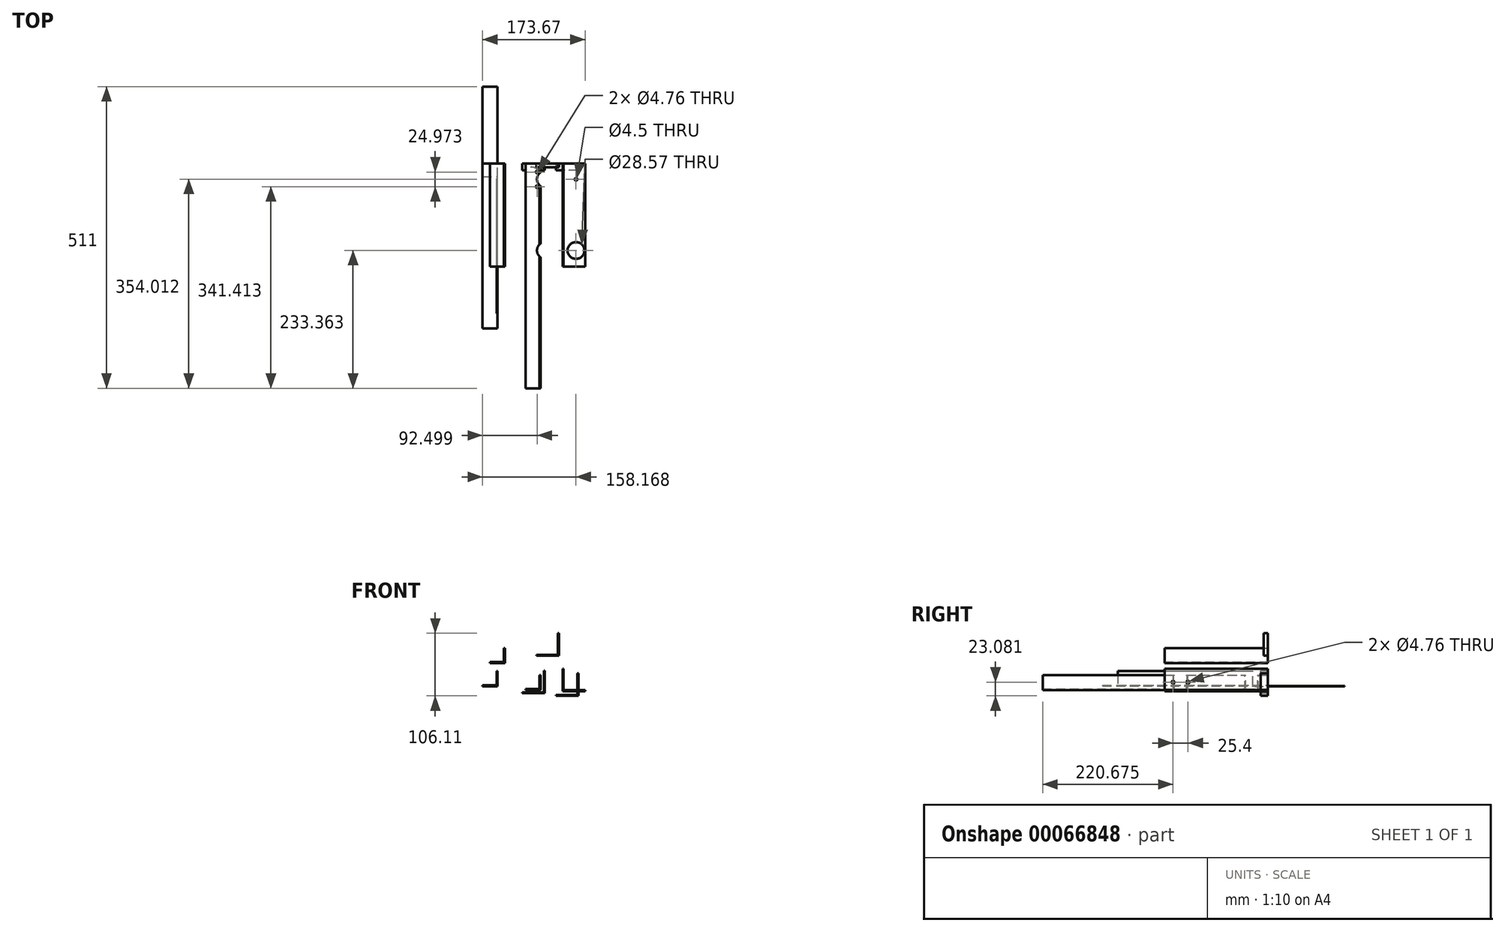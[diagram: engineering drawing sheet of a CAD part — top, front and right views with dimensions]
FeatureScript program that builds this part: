
annotation { "Feature Type Name" : "Feature", "Feature Type Description" : "" }
export const myFeature = defineFeature(function(context is Context, id is Id, definition is map)
    precondition{}
    {
        {
            assignVariable(context, id + "F0", {"name" : "angshooterl", "anyValue" : 12});
        }
        {
            var Q0;
            Q0=qCreatedBy(makeId("Front.planeOp"),FACE);
            var sketch = newSketch(context, id + "F1", { "sketchPlane" : qUnion([Q0])});
            skLineSegment(sketch, "E0.rect.bottom", {"start": v(12.7, 0.8) * mm, "end": v(-12.7, 0.8) * mm});
            skLineSegment(sketch, "E0.rect.top", {"start": v(12.7, -0.8) * mm, "end": v(-12.7, -0.8) * mm});
            skLineSegment(sketch, "E0.rect.left", {"start": v(12.7, 0.8) * mm, "end": v(12.7, -0.8) * mm});
            skLineSegment(sketch, "E0.rect.right", {"start": v(-12.7, 0.8) * mm, "end": v(-12.7, -0.8) * mm});
            skPoint(sketch, "E0.rect.middle", {"position": v(0, 0) * mm});
            skLineSegment(sketch, "E1.bottom", {"start": v(12.7, -0.8) * mm, "end": v(11.11, -0.8) * mm});
            skLineSegment(sketch, "E1.top", {"start": v(12.7, 24.6) * mm, "end": v(11.11, 24.6) * mm});
            skLineSegment(sketch, "E1.left", {"start": v(12.7, -0.8) * mm, "end": v(12.7, 24.6) * mm});
            skLineSegment(sketch, "E1.right", {"start": v(11.11, -0.8) * mm, "end": v(11.11, 24.6) * mm});
            skSolve(sketch);
        }
        {
            var Q0;
            Q0 = qSketchRegion(id + "F1", true);
            extrude(context, id + "F2", {"entities" : qUnion([Q0]), "depth" : 381 * mm});
        }
        {
            var Q0;
            Q0=qCreatedBy(makeId("Front.planeOp"),FACE);
            var sketch = newSketch(context, id + "F3", { "sketchPlane" : qUnion([Q0])});
            skLineSegment(sketch, "E2.rect.bottom", {"start": v(20.1, -4.5) * mm, "end": v(-18, -4.5) * mm});
            skLineSegment(sketch, "E2.rect.top", {"start": v(20.1, -6.09) * mm, "end": v(-18, -6.09) * mm});
            skLineSegment(sketch, "E2.rect.left", {"start": v(20.1, -4.5) * mm, "end": v(20.1, -6.09) * mm});
            skLineSegment(sketch, "E2.rect.right", {"start": v(-18, -4.5) * mm, "end": v(-18, -6.09) * mm});
            skPoint(sketch, "E2.rect.middle", {"position": v(1.06, -5.3) * mm});
            skLineSegment(sketch, "E3.bottom", {"start": v(20.1, -6.09) * mm, "end": v(18.52, -6.09) * mm});
            skLineSegment(sketch, "E3.top", {"start": v(20.1, 32.01) * mm, "end": v(18.52, 32.01) * mm});
            skLineSegment(sketch, "E3.left", {"start": v(20.1, -6.09) * mm, "end": v(20.1, 32.01) * mm});
            skLineSegment(sketch, "E3.right", {"start": v(18.52, -6.09) * mm, "end": v(18.52, 32.01) * mm});
            skSolve(sketch);
        }
        {
            var Q0;
            Q0 = qSketchRegion(id + "F3", true);
            extrude(context, id + "F4", {"entities" : qUnion([Q0]), "depth" : (getVariable(context, 'angshooterl')) * mm});
        }
        {
            var Q0;
            Q0=makeQuery(id+"F4.opExtrude","SWEPT_FACE",FACE,{"disambiguationData":[OSD([sQuery(id+"F3.wireOp",EDGE,"E2.rect.bottom")])]});
            var sketch = newSketch(context, id + "F5", { "sketchPlane" : qUnion([Q0])});
            skCircle(sketch, "E4", {"center": v(-2.48, -20.64) * mm, "radius": 14.29 * mm});
            skCircle(sketch, "E5", {"center": v(-2.36, -128.14) * mm, "radius": 14.29 * mm});
            skCircle(sketch, "E6", {"center": v(-1.24, -248.79) * mm, "radius": 14.29 * mm});
            skSolve(sketch);
        }
        {
            var Q0;
            Q0 = qSketchRegion(id + "F5", true);
            extrude(context, id + "F6", {"entities" : qUnion([Q0]), "operationType" : NewBodyOperationType.REMOVE, "endBound" : BoundingType.THROUGH_ALL, "oppositeDirection" : true, "depth" : 25.4 * mm});
        }
        {
            var Q0;
            Q0=qCreatedBy(makeId("Front.planeOp"),FACE);
            var sketch = newSketch(context, id + "F7", { "sketchPlane" : qUnion([Q0])});
            skLineSegment(sketch, "E7.rect.bottom", {"start": v(76.98, -8.97) * mm, "end": v(38.88, -8.97) * mm});
            skLineSegment(sketch, "E7.rect.top", {"start": v(76.98, -10.56) * mm, "end": v(38.88, -10.56) * mm});
            skLineSegment(sketch, "E7.rect.left", {"start": v(76.98, -8.97) * mm, "end": v(76.98, -10.56) * mm});
            skLineSegment(sketch, "E7.rect.right", {"start": v(38.88, -8.97) * mm, "end": v(38.88, -10.56) * mm});
            skPoint(sketch, "E7.rect.middle", {"position": v(57.93, -9.77) * mm});
            skLineSegment(sketch, "E8.bottom", {"start": v(76.98, -10.56) * mm, "end": v(75.4, -10.56) * mm});
            skLineSegment(sketch, "E8.top", {"start": v(76.98, 27.54) * mm, "end": v(75.4, 27.54) * mm});
            skLineSegment(sketch, "E8.left", {"start": v(76.98, -10.56) * mm, "end": v(76.98, 27.54) * mm});
            skLineSegment(sketch, "E8.right", {"start": v(75.4, -10.56) * mm, "end": v(75.4, 27.54) * mm});
            skSolve(sketch);
        }
        {
            var Q0;
            Q0 = qSketchRegion(id + "F7", true);
            extrude(context, id + "F8", {"entities" : qUnion([Q0]), "depth" : (getVariable(context, 'angshooterl')) * mm});
        }
        {
            var Q0;
            Q0=makeQuery(id+"F8.opExtrude","SWEPT_FACE",FACE,{"disambiguationData":[OSD([sQuery(id+"F7.wireOp",EDGE,"E7.rect.bottom")])]});
            var sketch = newSketch(context, id + "F9", { "sketchPlane" : qUnion([Q0])});
            skLineSegment(sketch, "E9", {"start": v(38.88, -152.4) * mm, "end": v(75.4, -152.4) * mm, "construction": true});
            skCircle(sketch, "E10.MirrorC", {"center": v(54.39, -284.16) * mm, "radius": 14.29 * mm});
            skCircle(sketch, "E11.MirrorC", {"center": v(54.39, -176.66) * mm, "radius": 14.29 * mm});
            skCircle(sketch, "E12.MirrorC", {"center": v(54.39, -56.01) * mm, "radius": 14.29 * mm});
            skSolve(sketch);
        }
        {
            var Q0;
            Q0 = qSketchRegion(id + "F9", true);
            extrude(context, id + "F10", {"entities" : qUnion([Q0]), "operationType" : NewBodyOperationType.REMOVE, "endBound" : BoundingType.THROUGH_ALL, "oppositeDirection" : true, "depth" : 25.4 * mm});
        }
        {
            var Q0;
            Q0=qCreatedBy(makeId("Front.planeOp"),FACE);
            var sketch = newSketch(context, id + "F11", { "sketchPlane" : qUnion([Q0])});
            skLineSegment(sketch, "E13.rect.bottom", {"start": v(-47.6, 46.62) * mm, "end": v(-73, 46.62) * mm});
            skLineSegment(sketch, "E13.rect.top", {"start": v(-47.6, 45.04) * mm, "end": v(-73, 45.04) * mm});
            skLineSegment(sketch, "E13.rect.left", {"start": v(-47.6, 46.62) * mm, "end": v(-47.6, 45.04) * mm});
            skLineSegment(sketch, "E13.rect.right", {"start": v(-73, 46.62) * mm, "end": v(-73, 45.04) * mm});
            skPoint(sketch, "E13.rect.middle", {"position": v(-60.3, 45.83) * mm});
            skLineSegment(sketch, "E14.bottom", {"start": v(-47.6, 45.04) * mm, "end": v(-49.2, 45.04) * mm});
            skLineSegment(sketch, "E14.top", {"start": v(-47.6, 70.44) * mm, "end": v(-49.2, 70.44) * mm});
            skLineSegment(sketch, "E14.left", {"start": v(-47.6, 45.04) * mm, "end": v(-47.6, 70.44) * mm});
            skLineSegment(sketch, "E14.right", {"start": v(-49.2, 45.04) * mm, "end": v(-49.2, 70.44) * mm});
            skSolve(sketch);
        }
        {
            var Q0;
            Q0 = qSketchRegion(id + "F11", true);
            extrude(context, id + "F12", {"entities" : qUnion([Q0]), "depth" : 174.62 * mm});
        }
        {
            assignVariable(context, id + "F13", {"name" : "ShooterLength2Wh", "anyValue" : 6.38 + .5});
        }
        {
            var Q0;
            Q0=qCreatedBy(makeId("Front.planeOp"),FACE);
            var sketch = newSketch(context, id + "F14", { "sketchPlane" : qUnion([Q0])});
            skLineSegment(sketch, "E15.rect.bottom", {"start": v(43.74, 59.04) * mm, "end": v(5.64, 59.04) * mm});
            skLineSegment(sketch, "E15.rect.top", {"start": v(43.74, 57.45) * mm, "end": v(5.64, 57.45) * mm});
            skLineSegment(sketch, "E15.rect.left", {"start": v(43.74, 59.04) * mm, "end": v(43.74, 57.45) * mm});
            skLineSegment(sketch, "E15.rect.right", {"start": v(5.64, 59.04) * mm, "end": v(5.64, 57.45) * mm});
            skPoint(sketch, "E15.rect.middle", {"position": v(24.7, 58.24) * mm});
            skLineSegment(sketch, "E16.bottom", {"start": v(43.74, 57.45) * mm, "end": v(42.15, 57.45) * mm});
            skLineSegment(sketch, "E16.top", {"start": v(43.74, 95.55) * mm, "end": v(42.15, 95.55) * mm});
            skLineSegment(sketch, "E16.left", {"start": v(43.74, 57.45) * mm, "end": v(43.74, 95.55) * mm});
            skLineSegment(sketch, "E16.right", {"start": v(42.15, 57.45) * mm, "end": v(42.15, 95.55) * mm});
            skSolve(sketch);
        }
        {
            var Q0;
            Q0 = qSketchRegion(id + "F14", true);
            extrude(context, id + "F15", {"entities" : qUnion([Q0]), "depth" : (getVariable(context, 'ShooterLength2Wh')) * mm});
        }
        {
            var Q0;
            Q0=makeQuery(id+"F15.opExtrude","SWEPT_FACE",FACE,{"disambiguationData":[OSD([sQuery(id+"F14.wireOp",EDGE,"E15.rect.bottom")])]});
            var sketch = newSketch(context, id + "F16", { "sketchPlane" : qUnion([Q0])});
            skCircle(sketch, "E17", {"center": v(21.15, -26.99) * mm, "radius": 14.29 * mm});
            skCircle(sketch, "E18", {"center": v(21.15, -147.64) * mm, "radius": 14.29 * mm});
            skLineSegment(sketch, "E19.0", {"start": v(7.24, -14.61) * mm, "end": v(31.99, -14.61) * mm, "construction": true});
            skLineSegment(sketch, "E19.1", {"start": v(31.99, -14.61) * mm, "end": v(31.99, -39.44) * mm, "construction": true});
            skLineSegment(sketch, "E19.3", {"start": v(7.24, -39.59) * mm, "end": v(7.24, -14.61) * mm, "construction": true});
            skCircle(sketch, "E20", {"center": v(31.99, -14.61) * mm, "radius": 2.38 * mm});
            skCircle(sketch, "E21", {"center": v(31.99, -39.44) * mm, "radius": 2.38 * mm});
            skCircle(sketch, "E22", {"center": v(7.24, -39.59) * mm, "radius": 2.38 * mm});
            skCircle(sketch, "E23", {"center": v(7.24, -14.61) * mm, "radius": 2.38 * mm});
            skLineSegment(sketch, "E24", {"start": v(21.15, -26.99) * mm, "end": v(21.15, -147.64) * mm, "construction": true});
            skLineSegment(sketch, "E25", {"start": v(21.15, -87.31) * mm, "end": v(32.9, -87.31) * mm, "construction": true});
            skSolve(sketch);
        }
        {
            var Q0;
            Q0 = qSketchRegion(id + "F16", true);
            extrude(context, id + "F17", {"entities" : qUnion([Q0]), "operationType" : NewBodyOperationType.REMOVE, "endBound" : BoundingType.THROUGH_ALL, "oppositeDirection" : true, "depth" : 25.4 * mm});
        }
        {
            var Q0;
            Q0=qCreatedBy(makeId("Front.planeOp"),FACE);
            var sketch = newSketch(context, id + "F18", { "sketchPlane" : qUnion([Q0])});
            skLineSegment(sketch, "E26.rect.bottom", {"start": v(-59.86, 7.45) * mm, "end": v(-85.26, 7.45) * mm});
            skLineSegment(sketch, "E26.rect.top", {"start": v(-59.86, 5.86) * mm, "end": v(-85.26, 5.86) * mm});
            skLineSegment(sketch, "E26.rect.left", {"start": v(-59.86, 7.45) * mm, "end": v(-59.86, 5.86) * mm});
            skLineSegment(sketch, "E26.rect.right", {"start": v(-85.26, 7.45) * mm, "end": v(-85.26, 5.86) * mm});
            skPoint(sketch, "E26.rect.middle", {"position": v(-72.56, 6.66) * mm});
            skLineSegment(sketch, "E27.bottom", {"start": v(-59.86, 5.86) * mm, "end": v(-61.44, 5.86) * mm});
            skLineSegment(sketch, "E27.top", {"start": v(-59.86, 31.26) * mm, "end": v(-61.44, 31.26) * mm});
            skLineSegment(sketch, "E27.left", {"start": v(-59.86, 5.86) * mm, "end": v(-59.86, 31.26) * mm});
            skLineSegment(sketch, "E27.right", {"start": v(-61.44, 5.86) * mm, "end": v(-61.44, 31.26) * mm});
            skSolve(sketch);
        }
        {
            var Q0;
            Q0 = qSketchRegion(id + "F18", true);
            extrude(context, id + "F19", {"entities" : qUnion([Q0]), "depth" : 279.4 * mm});
        }
        {
            var Q0;
            Q0=makeQuery(id+"F19.opExtrude","SWEPT_FACE",FACE,{"disambiguationData":[OSD([sQuery(id+"F18.wireOp",EDGE,"E27.right")])]});
            var sketch = newSketch(context, id + "F20", { "sketchPlane" : qUnion([Q0])});
            skLineSegment(sketch, "E28.bottom", {"start": v(279.4, 31.26) * mm, "end": v(254, 31.26) * mm});
            skLineSegment(sketch, "E28.top", {"start": v(279.4, 7.45) * mm, "end": v(254, 7.45) * mm});
            skLineSegment(sketch, "E28.left", {"start": v(279.4, 31.26) * mm, "end": v(279.4, 7.45) * mm});
            skLineSegment(sketch, "E28.right", {"start": v(254, 31.26) * mm, "end": v(254, 7.45) * mm});
            skLineSegment(sketch, "E29.bottom", {"start": v(0, 7.45) * mm, "end": v(25.4, 7.45) * mm});
            skLineSegment(sketch, "E29.top", {"start": v(0, 31.26) * mm, "end": v(25.4, 31.26) * mm});
            skLineSegment(sketch, "E29.left", {"start": v(0, 7.45) * mm, "end": v(0, 31.26) * mm});
            skLineSegment(sketch, "E29.right", {"start": v(25.4, 7.45) * mm, "end": v(25.4, 31.26) * mm});
            skSolve(sketch);
        }
        {
            var Q0;
            Q0 = qSketchRegion(id + "F20", true);
            extrude(context, id + "F21", {"entities" : qUnion([Q0]), "operationType" : NewBodyOperationType.REMOVE, "oppositeDirection" : true, "depth" : 25.4 * mm});
        }
        {
            var Q0;
            Q0=makeQuery(id+"F19.opExtrude","SWEPT_FACE",FACE,{"disambiguationData":[OSD([sQuery(id+"F18.wireOp",EDGE,"E26.rect.top"),sQuery(id+"F18.wireOp",EDGE,"E27.bottom")])]});
            var sketch = newSketch(context, id + "F22", { "sketchPlane" : qUnion([Q0])});
            skLineSegment(sketch, "E30.bottom", {"start": v(-85.26, 22.4) * mm, "end": v(-59.86, 22.4) * mm});
            skLineSegment(sketch, "E30.top", {"start": v(-85.26, -130) * mm, "end": v(-59.86, -130) * mm});
            skLineSegment(sketch, "E30.left", {"start": v(-85.26, 22.4) * mm, "end": v(-85.26, -130) * mm});
            skLineSegment(sketch, "E30.right", {"start": v(-59.86, 22.4) * mm, "end": v(-59.86, -130) * mm});
            skSolve(sketch);
        }
        {
            var Q0;
            Q0 = qSketchRegion(id + "F22", true);
            extrude(context, id + "F23", {"entities" : qUnion([Q0]), "operationType" : NewBodyOperationType.ADD, "depth" : 0.76 * mm});
        }
        {
            var Q0;
            Q0=qCreatedBy(makeId("Front.planeOp"),FACE);
            var sketch = newSketch(context, id + "F24", { "sketchPlane" : qUnion([Q0])});
            skLineSegment(sketch, "E31.rect.bottom", {"start": v(88.41, -0.98) * mm, "end": v(50.31, -0.98) * mm});
            skLineSegment(sketch, "E31.rect.top", {"start": v(88.41, -2.57) * mm, "end": v(50.31, -2.57) * mm});
            skLineSegment(sketch, "E31.rect.left", {"start": v(88.41, -0.98) * mm, "end": v(88.41, -2.57) * mm});
            skLineSegment(sketch, "E31.rect.right", {"start": v(50.31, -0.98) * mm, "end": v(50.31, -2.57) * mm});
            skPoint(sketch, "E31.rect.middle", {"position": v(69.36, -1.77) * mm});
            skLineSegment(sketch, "E32.bottom", {"start": v(88.41, -2.57) * mm, "end": v(86.83, -2.57) * mm});
            skLineSegment(sketch, "E33", {"start": v(69.36, -0.98) * mm, "end": v(69.36, -2.57) * mm, "construction": true});
            skLineSegment(sketch, "E34.MirrorCS", {"start": v(50.31, 35.53) * mm, "end": v(51.9, 35.53) * mm});
            skLineSegment(sketch, "E35.MirrorCS", {"start": v(50.31, -2.57) * mm, "end": v(51.9, -2.57) * mm});
            skLineSegment(sketch, "E36.MirrorCS", {"start": v(50.31, -2.57) * mm, "end": v(50.31, 35.53) * mm});
            skLineSegment(sketch, "E37.MirrorCS", {"start": v(51.9, -2.57) * mm, "end": v(51.9, 35.53) * mm});
            skSolve(sketch);
        }
        {
            var Q0;
            Q0 = qSketchRegion(id + "F24", true);
            extrude(context, id + "F25", {"entities" : qUnion([Q0]), "depth" : 174.62 * mm});
        }
        {
            var Q0;
            Q0=makeQuery(id+"F25.opExtrude","SWEPT_FACE",FACE,{"disambiguationData":[OSD([sQuery(id+"F24.wireOp",EDGE,"E31.rect.bottom")])]});
            var sketch = newSketch(context, id + "F26", { "sketchPlane" : qUnion([Q0])});
            skCircle(sketch, "E38", {"center": v(72.9, -147.64) * mm, "radius": 14.29 * mm});
            skCircle(sketch, "E39", {"center": v(72.9, -26.99) * mm, "radius": 2.25 * mm});
            skCircle(sketch, "E40", {"center": v(214.06, -106.45) * mm, "radius": 2.38 * mm});
            skCircle(sketch, "E41", {"center": v(239.46, -106.45) * mm, "radius": 2.38 * mm});
            skLineSegment(sketch, "E42", {"start": v(214.06, -106.45) * mm, "end": v(239.46, -106.45) * mm, "construction": true});
            skSolve(sketch);
        }
        {
            var Q0;
            Q0 = qSketchRegion(id + "F26", true);
            extrude(context, id + "F27", {"entities" : qUnion([Q0]), "operationType" : NewBodyOperationType.REMOVE, "endBound" : BoundingType.THROUGH_ALL, "oppositeDirection" : true, "depth" : 25.4 * mm});
        }
        {
            var Q0;
            Q0=makeQuery(id+"F15.opExtrude","SWEPT_FACE",FACE,{"disambiguationData":[OSD([sQuery(id+"F14.wireOp",EDGE,"E16.right")])]});
            var sketch = newSketch(context, id + "F28", { "sketchPlane" : qUnion([Q0])});
            skCircle(sketch, "E43", {"center": v(134.92, 72.53) * mm, "radius": 2.38 * mm});
            skCircle(sketch, "E44", {"center": v(160.32, 72.53) * mm, "radius": 2.38 * mm});
            skLineSegment(sketch, "E45", {"start": v(134.92, 72.53) * mm, "end": v(160.32, 72.53) * mm, "construction": true});
            skPoint(sketch, "E46", {"position": v(147.62, 72.53) * mm});
            skSolve(sketch);
        }
        {
            var Q0;
            Q0 = qSketchRegion(id + "F28", true);
            extrude(context, id + "F29", {"entities" : qUnion([Q0]), "operationType" : NewBodyOperationType.REMOVE, "endBound" : BoundingType.THROUGH_ALL, "oppositeDirection" : true, "depth" : 25.4 * mm});
        }
        {
            var Q0;
            Q0=makeQuery(id+"F25.opExtrude","SWEPT_FACE",FACE,{"disambiguationData":[OSD([sQuery(id+"F24.wireOp",EDGE,"E37.MirrorCS")])]});
            var sketch = newSketch(context, id + "F30", { "sketchPlane" : qUnion([Q0])});
            skCircle(sketch, "E47", {"center": v(-160.32, 12.52) * mm, "radius": 2.38 * mm});
            skCircle(sketch, "E48", {"center": v(-134.92, 12.52) * mm, "radius": 2.38 * mm});
            skLineSegment(sketch, "E49", {"start": v(-160.32, 12.52) * mm, "end": v(-134.92, 12.52) * mm, "construction": true});
            skSolve(sketch);
        }
        {
            var Q0;
            Q0 = qSketchRegion(id + "F30", true);
            extrude(context, id + "F31", {"entities" : qUnion([Q0]), "operationType" : NewBodyOperationType.REMOVE, "oppositeDirection" : true, "depth" : 25.4 * mm});
        }
    });
